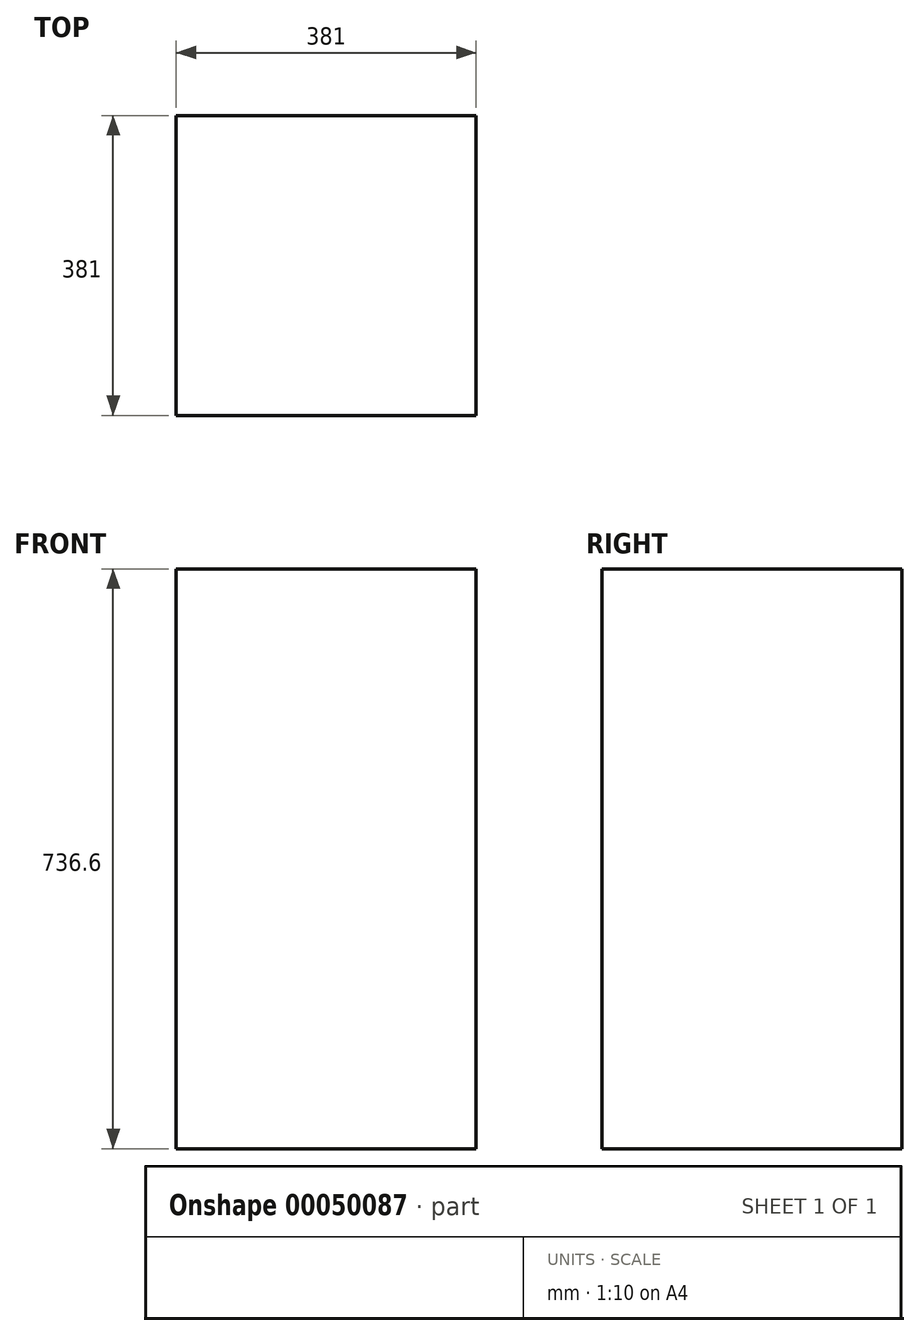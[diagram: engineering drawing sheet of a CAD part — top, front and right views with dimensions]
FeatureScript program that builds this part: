
annotation { "Feature Type Name" : "Feature", "Feature Type Description" : "" }
export const myFeature = defineFeature(function(context is Context, id is Id, definition is map)
    precondition{}
    {
        {
            var Q0;
            Q0=qCreatedBy(makeId("Top.planeOp"),FACE);
            var sketch = newSketch(context, id + "F0", { "sketchPlane" : qUnion([Q0])});
            skLineSegment(sketch, "E0.bottom", {"start": v(-190.5, 190.5) * mm, "end": v(190.5, 190.5) * mm});
            skLineSegment(sketch, "E0.top", {"start": v(-190.5, -190.5) * mm, "end": v(190.5, -190.5) * mm});
            skLineSegment(sketch, "E0.left", {"start": v(-190.5, 190.5) * mm, "end": v(-190.5, -190.5) * mm});
            skLineSegment(sketch, "E0.right", {"start": v(190.5, 190.5) * mm, "end": v(190.5, -190.5) * mm});
            skSolve(sketch);
        }
        {
            var Q0;
            Q0 = qSketchRegion(id + "F0", true);
            extrude(context, id + "F1", {"entities" : qUnion([Q0]), "depth" : 736.6 * mm});
        }
    });
